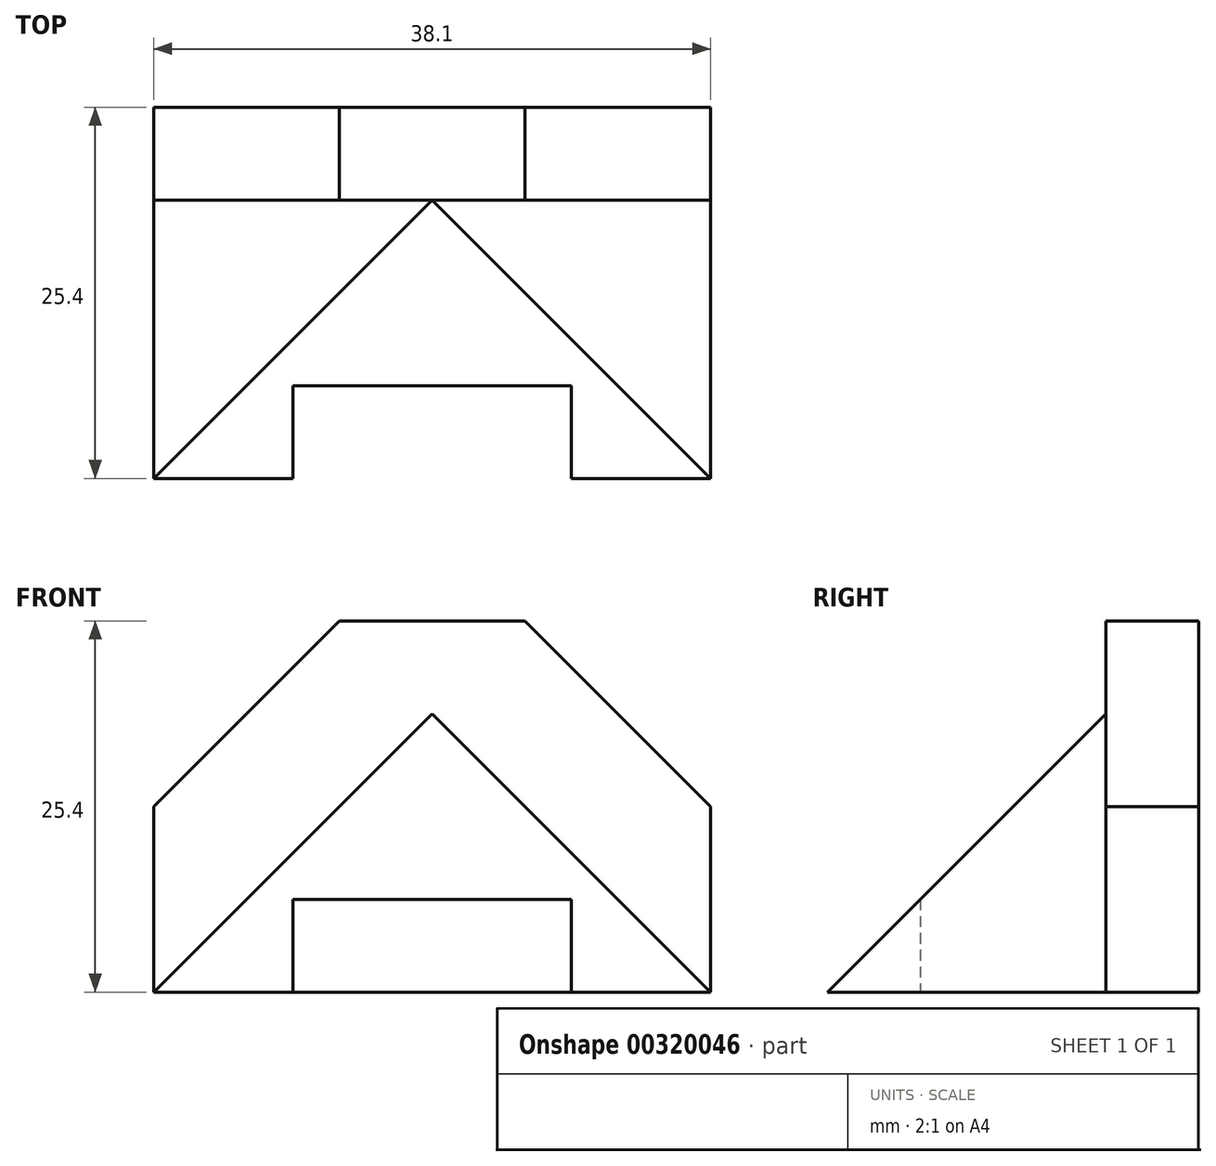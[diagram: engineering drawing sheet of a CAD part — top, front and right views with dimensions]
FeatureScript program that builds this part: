
annotation { "Feature Type Name" : "Feature", "Feature Type Description" : "" }
export const myFeature = defineFeature(function(context is Context, id is Id, definition is map)
    precondition{}
    {
        {
            var Q0;
            Q0=qCreatedBy(makeId("Front.planeOp"),FACE);
            var sketch = newSketch(context, id + "F0", { "sketchPlane" : qUnion([Q0])});
            skLineSegment(sketch, "E0", {"start": v(0, 0) * mm, "end": v(38.1, 0) * mm});
            skLineSegment(sketch, "E1", {"start": v(38.1, 0) * mm, "end": v(38.1, 25.4) * mm});
            skLineSegment(sketch, "E2", {"start": v(38.1, 25.4) * mm, "end": v(0, 25.4) * mm});
            skLineSegment(sketch, "E3", {"start": v(0, 25.4) * mm, "end": v(0, 0) * mm});
            skSolve(sketch);
        }
        {
            var Q0;
            Q0 = qSketchRegion(id + "F0", true);
            extrude(context, id + "F1", {"entities" : qUnion([Q0]), "depth" : 25.4 * mm});
        }
        {
            var Q0;
            Q0=makeQuery(id+"F1.opExtrude","CAP_FACE",FACE,{"disambiguationData":[OSD([sQuery(id+"F0.wireOp",EDGE,"E0"),sQuery(id+"F0.wireOp",EDGE,"E1"),sQuery(id+"F0.wireOp",EDGE,"E2"),sQuery(id+"F0.wireOp",EDGE,"E3")])],"isStart":false});
            var sketch = newSketch(context, id + "F2", { "sketchPlane" : qUnion([Q0])});
            skLineSegment(sketch, "E4", {"start": v(0, 25.4) * mm, "end": v(12.7, 25.4) * mm});
            skLineSegment(sketch, "E5", {"start": v(12.7, 25.4) * mm, "end": v(0, 25.4) * mm});
            skLineSegment(sketch, "E6", {"start": v(0, 25.4) * mm, "end": v(0, 12.7) * mm});
            skLineSegment(sketch, "E7", {"start": v(0, 12.7) * mm, "end": v(12.7, 25.4) * mm});
            skLineSegment(sketch, "E8", {"start": v(38.1, 25.4) * mm, "end": v(25.4, 25.4) * mm});
            skLineSegment(sketch, "E9", {"start": v(25.4, 25.4) * mm, "end": v(38.1, 25.4) * mm});
            skLineSegment(sketch, "E10", {"start": v(38.1, 12.7) * mm, "end": v(38.1, 25.4) * mm});
            skLineSegment(sketch, "E11", {"start": v(25.4, 25.4) * mm, "end": v(38.1, 12.7) * mm});
            skSolve(sketch);
        }
        {
            var Q0;
            Q0 = qSketchRegion(id + "F2", true);
            extrude(context, id + "F3", {"entities" : qUnion([Q0]), "operationType" : NewBodyOperationType.REMOVE, "oppositeDirection" : true, "depth" : 25.4 * mm});
        }
        {
            var Q0;
            Q0=makeQuery(id+"F1.opExtrude","CAP_FACE",FACE,{"disambiguationData":[OSD([sQuery(id+"F0.wireOp",EDGE,"E0"),sQuery(id+"F0.wireOp",EDGE,"E1"),sQuery(id+"F0.wireOp",EDGE,"E2"),sQuery(id+"F0.wireOp",EDGE,"E3")])],"isStart":false});
            var sketch = newSketch(context, id + "F4", { "sketchPlane" : qUnion([Q0])});
            skLineSegment(sketch, "E12", {"start": v(19.05, 0) * mm, "end": v(19.05, 19.05) * mm});
            skLineSegment(sketch, "E13", {"start": v(19.05, 19.05) * mm, "end": v(0, 0) * mm});
            skLineSegment(sketch, "E14", {"start": v(0, 0) * mm, "end": v(0, 12.7) * mm});
            skLineSegment(sketch, "E15", {"start": v(0, 12.7) * mm, "end": v(12.7, 25.4) * mm});
            skLineSegment(sketch, "E16", {"start": v(12.7, 25.4) * mm, "end": v(25.4, 25.4) * mm});
            skLineSegment(sketch, "E17", {"start": v(25.4, 25.4) * mm, "end": v(38.1, 12.7) * mm});
            skLineSegment(sketch, "E18", {"start": v(38.1, 12.7) * mm, "end": v(38.1, 0) * mm});
            skLineSegment(sketch, "E19", {"start": v(38.1, 0) * mm, "end": v(19.05, 19.05) * mm});
            skSolve(sketch);
        }
        {
            var Q0;
            Q0 = qSketchRegion(id + "F4", true);
            extrude(context, id + "F5", {"entities" : qUnion([Q0]), "operationType" : NewBodyOperationType.REMOVE, "oppositeDirection" : true, "depth" : 19.05 * mm});
        }
        {
            var Q0;
            Q0=qCreatedBy(makeId("Right.planeOp"),FACE);
            var sketch = newSketch(context, id + "F6", { "sketchPlane" : qUnion([Q0])});
            skLineSegment(sketch, "E20", {"start": v(0, 0) * mm, "end": v(-25.4, 0) * mm});
            skLineSegment(sketch, "E21", {"start": v(-25.4, 0) * mm, "end": v(-25.4, 19.05) * mm});
            skLineSegment(sketch, "E22", {"start": v(-25.4, 19.05) * mm, "end": v(-6.35, 19.05) * mm});
            skLineSegment(sketch, "E23", {"start": v(-6.35, 19.05) * mm, "end": v(-25.4, 0) * mm});
            skSolve(sketch);
        }
        {
            var Q0;
            Q0 = qSketchRegion(id + "F6", true);
            extrude(context, id + "F7", {"entities" : qUnion([Q0]), "operationType" : NewBodyOperationType.REMOVE, "depth" : 558.8 * mm});
        }
        {
            var Q0;
            Q0=makeQuery(id+"F1.opExtrude","SWEPT_FACE",FACE,{"disambiguationData":[OSD([sQuery(id+"F0.wireOp",EDGE,"E0")])]});
            var sketch = newSketch(context, id + "F8", { "sketchPlane" : qUnion([Q0])});
            skLineSegment(sketch, "E24", {"start": v(0, 25.4) * mm, "end": v(9.53, 25.4) * mm});
            skLineSegment(sketch, "E25", {"start": v(9.53, 25.4) * mm, "end": v(9.53, 19.05) * mm});
            skLineSegment(sketch, "E26", {"start": v(9.53, 19.05) * mm, "end": v(28.57, 19.05) * mm});
            skLineSegment(sketch, "E27", {"start": v(28.57, 19.05) * mm, "end": v(28.57, 25.4) * mm});
            skLineSegment(sketch, "E28", {"start": v(28.57, 25.4) * mm, "end": v(9.53, 25.4) * mm});
            skLineSegment(sketch, "E29", {"start": v(28.57, 25.4) * mm, "end": v(38.1, 25.4) * mm});
            skSolve(sketch);
        }
        {
            var Q0;
            Q0 = qSketchRegion(id + "F8", true);
            extrude(context, id + "F9", {"entities" : qUnion([Q0]), "operationType" : NewBodyOperationType.REMOVE, "oppositeDirection" : true, "depth" : 25.4 * mm});
        }
    });
